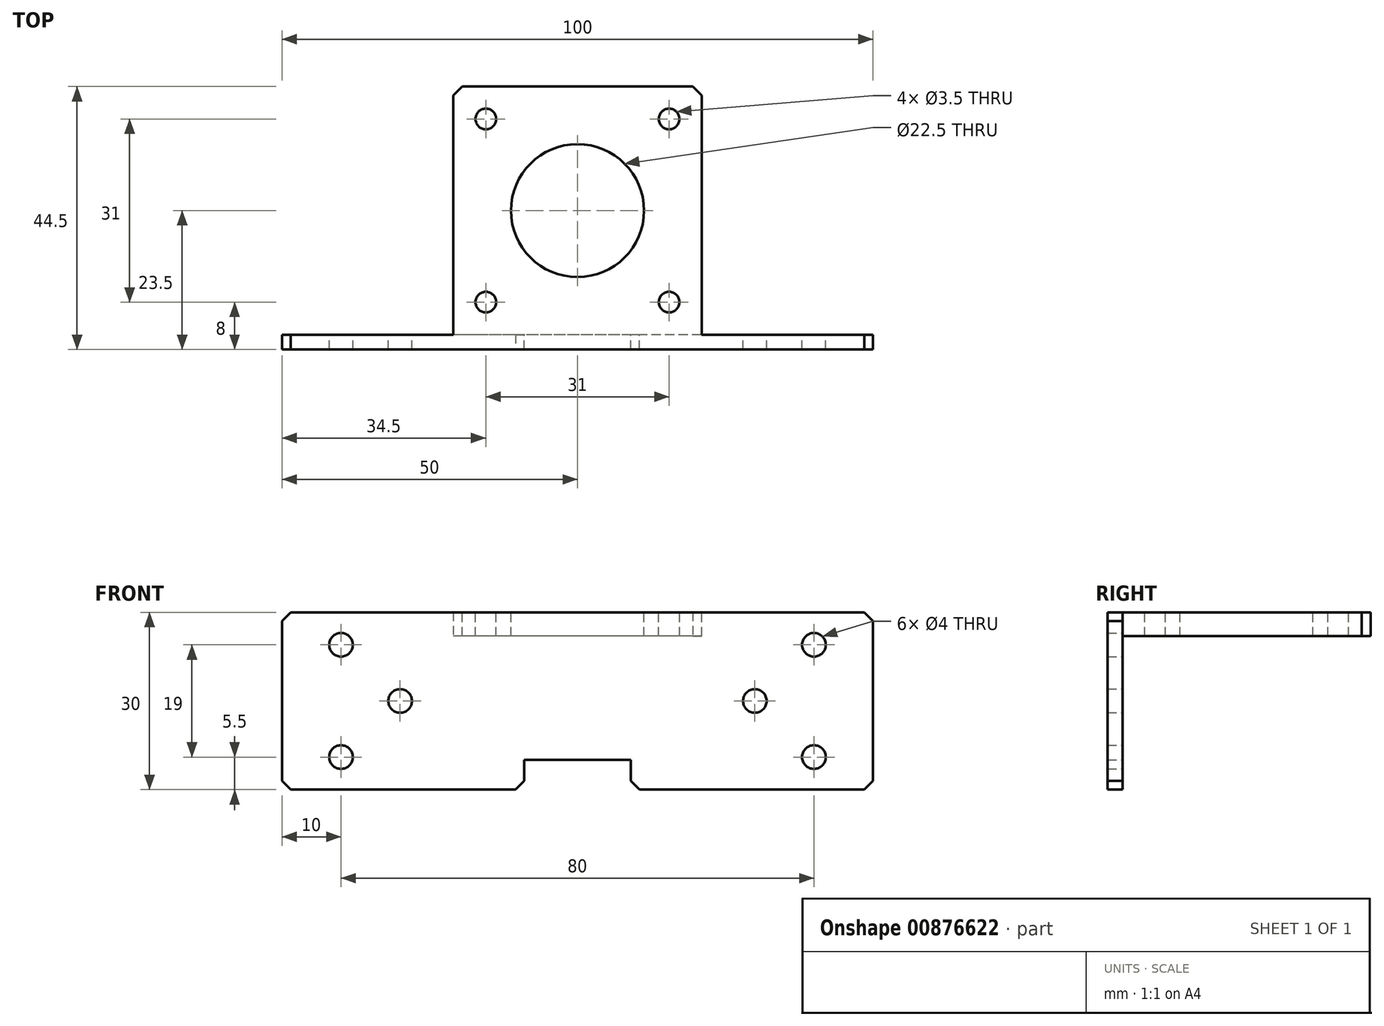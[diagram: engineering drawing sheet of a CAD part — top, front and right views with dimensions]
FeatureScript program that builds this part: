
annotation { "Feature Type Name" : "Feature", "Feature Type Description" : "" }
export const myFeature = defineFeature(function(context is Context, id is Id, definition is map)
    precondition{}
    {
        {
            var Q0;
            Q0=qCreatedBy(makeId("Top.planeOp"),FACE);
            var sketch = newSketch(context, id + "F0", { "sketchPlane" : qUnion([Q0])});
            skLineSegment(sketch, "E0.bottom", {"start": v(21, 21) * mm, "end": v(-21, 21) * mm});
            skLineSegment(sketch, "E0.top", {"start": v(21, -21) * mm, "end": v(-21, -21) * mm});
            skLineSegment(sketch, "E0.left", {"start": v(21, 21) * mm, "end": v(21, -21) * mm});
            skLineSegment(sketch, "E0.right", {"start": v(-21, 21) * mm, "end": v(-21, -21) * mm});
            skPoint(sketch, "E0.middle", {"position": v(0, 0) * mm});
            skLineSegment(sketch, "E1.0", {"start": v(21, 15.5) * mm, "end": v(-21, 15.5) * mm, "construction": true});
            skLineSegment(sketch, "E2.0", {"start": v(21, -15.5) * mm, "end": v(-21, -15.5) * mm, "construction": true});
            skLineSegment(sketch, "E3", {"start": v(-21, 0) * mm, "end": v(21, 0) * mm, "construction": true});
            skLineSegment(sketch, "E4", {"start": v(0, 21) * mm, "end": v(0, -21) * mm, "construction": true});
            skCircle(sketch, "E5", {"center": v(0, 0) * mm, "radius": 11.25 * mm});
            skLineSegment(sketch, "E6.0", {"start": v(-15.5, 21) * mm, "end": v(-15.5, -21) * mm, "construction": true});
            skLineSegment(sketch, "E7.0", {"start": v(15.5, 21) * mm, "end": v(15.5, -21) * mm, "construction": true});
            skCircle(sketch, "E8", {"center": v(-15.5, 15.5) * mm, "radius": 1.75 * mm});
            skCircle(sketch, "E9.MirrorC", {"center": v(15.5, 15.5) * mm, "radius": 1.75 * mm});
            skCircle(sketch, "E10.MirrorC", {"center": v(15.5, -15.5) * mm, "radius": 1.75 * mm});
            skCircle(sketch, "E11.MirrorC", {"center": v(-15.5, -15.5) * mm, "radius": 1.75 * mm});
            skSolve(sketch);
        }
        {
            var Q0;
            Q0=makeQuery(id+"F0.imprint","IMPRINT",FACE,{"disambiguationData":[TD([[makeQuery(id+"F0.imprint","IMPRINT",EDGE,{"derivedFrom":sQuery(id+"F0.wireOp",EDGE,"E0.bottom")}),1.0]])]});
            var Q1;
            Q1=makeQuery(id+"F0.imprint","IMPRINT",FACE,{"disambiguationData":[TD([[makeQuery(id+"F0.imprint","IMPRINT",EDGE,{"derivedFrom":sQuery(id+"F0.wireOp",EDGE,"HWjcr97h-bGiZ-oV4i-kZyB-UvR0nVrvKp9y")}),1.0]])]});
            extrude(context, id + "F1", {"entities" : qUnion([Q0, Q1]), "oppositeDirection" : true, "depth" : 4 * mm, "offsetDistance" : 25 * mm});
        }
        {
            var Q0;
            Q0=makeQuery(id+"F1.opExtrude","SWEPT_FACE",FACE,{"disambiguationData":[OSD([sQuery(id+"F0.wireOp",EDGE,"E0.top")])]});
            var sketch = newSketch(context, id + "F2", { "sketchPlane" : qUnion([Q0])});
            skLineSegment(sketch, "E12", {"start": v(0, 0) * mm, "end": v(0, -30) * mm, "construction": true});
            skLineSegment(sketch, "E13.bottom", {"start": v(50, 0) * mm, "end": v(-50, 0) * mm});
            skLineSegment(sketch, "E13.top", {"start": v(50, -30) * mm, "end": v(-50, -30) * mm});
            skLineSegment(sketch, "E13.left", {"start": v(50, 0) * mm, "end": v(50, -30) * mm});
            skLineSegment(sketch, "E13.right", {"start": v(-50, 0) * mm, "end": v(-50, -30) * mm});
            skPoint(sketch, "E13.middle", {"position": v(0, -15) * mm});
            skLineSegment(sketch, "E14.0", {"start": v(-40, 0) * mm, "end": v(-40, -30) * mm, "construction": true});
            skLineSegment(sketch, "E15.0", {"start": v(44, 0) * mm, "end": v(44, -30) * mm, "construction": true});
            skLineSegment(sketch, "E16.0", {"start": v(50, -5.5) * mm, "end": v(-50, -5.5) * mm, "construction": true});
            skLineSegment(sketch, "E17.0", {"start": v(70, -24.5) * mm, "end": v(-50, -24.5) * mm, "construction": true});
            skCircle(sketch, "E18", {"center": v(-40, -5.5) * mm, "radius": 2 * mm});
            skLineSegment(sketch, "E19", {"start": v(-50, -15) * mm, "end": v(50, -15) * mm, "construction": true});
            skCircle(sketch, "E20.MirrorC", {"center": v(40, -5.5) * mm, "radius": 2 * mm});
            skCircle(sketch, "E21.MirrorC", {"center": v(40, -24.5) * mm, "radius": 2 * mm});
            skCircle(sketch, "E22.MirrorC", {"center": v(-40, -24.5) * mm, "radius": 2 * mm});
            skLineSegment(sketch, "E23.0", {"start": v(-30, 0) * mm, "end": v(-30, -30) * mm, "construction": true});
            skCircle(sketch, "E24", {"center": v(-30, -15) * mm, "radius": 2 * mm});
            skCircle(sketch, "E25.MirrorC", {"center": v(30, -15) * mm, "radius": 2 * mm});
            skLineSegment(sketch, "E26.bottom", {"start": v(9, -25) * mm, "end": v(-9, -25) * mm});
            skLineSegment(sketch, "E26.left", {"start": v(9, -25) * mm, "end": v(9, -30) * mm});
            skLineSegment(sketch, "E26.right", {"start": v(-9, -25) * mm, "end": v(-9, -30) * mm});
            skPoint(sketch, "E26.middle", {"position": v(0, -30) * mm});
            skPoint(sketch, "E27", {"position": v(0, -25) * mm});
            skSolve(sketch);
        }
        {
            var Q0;
            {var subQ1=sQuery(id+"F2.wireOp",EDGE,"E13.left");Q0=makeQuery(id+"F2.imprint","IMPRINT",FACE,{"disambiguationData":[TD([[makeQuery(id+"F2.imprint","IMPRINT",EDGE,{"derivedFrom":subQ1}),-1.0]])]});}
            var Q1;
            {var subQ1=sQuery(id+"F0.wireOp",EDGE,"E0.top");Q1=makeQuery(id+"F2.imprint","IMPRINT",FACE,{"disambiguationData":[TD([[makeQuery(id+"F2.imprint","IMPRINT",EDGE,{"derivedFrom":makeQuery(id+"F1.opExtrude","CAP_EDGE",EDGE,{"disambiguationData":[OSD([subQ1])],"isStart":false})}),-1.0]])]});}
            extrude(context, id + "F3", {"entities" : qUnion([Q0, Q1]), "operationType" : NewBodyOperationType.ADD, "depth" : 2.5 * mm, "offsetDistance" : 25 * mm});
        }
        {
            var Q0;
            Q0=makeQuery(id+"F1.opExtrude","SWEPT_EDGE",EDGE,{"disambiguationData":[OSD([sQuery(id+"F0.wireOp",EDGE,"E0.bottom"),sQuery(id+"F0.wireOp",EDGE,"E0.right")])]});
            var Q1;
            Q1=makeQuery(id+"F1.opExtrude","SWEPT_EDGE",EDGE,{"disambiguationData":[OSD([sQuery(id+"F0.wireOp",EDGE,"E0.bottom"),sQuery(id+"F0.wireOp",EDGE,"E0.left")])]});
            var Q2;
            Q2=makeQuery(id+"F3.opExtrude","SWEPT_EDGE",EDGE,{"disambiguationData":[OSD([sQuery(id+"F2.wireOp",EDGE,"E13.bottom"),sQuery(id+"F2.wireOp",EDGE,"E13.right")])]});
            var Q3;
            Q3=makeQuery(id+"F3.opExtrude","SWEPT_EDGE",EDGE,{"disambiguationData":[OSD([sQuery(id+"F2.wireOp",EDGE,"E13.top"),sQuery(id+"F2.wireOp",EDGE,"E13.right")])]});
            var Q4;
            Q4=makeQuery(id+"F3.opExtrude","SWEPT_EDGE",EDGE,{"disambiguationData":[OSD([sQuery(id+"F2.wireOp",EDGE,"E13.top"),sQuery(id+"F2.wireOp",EDGE,"E13.left")])]});
            var Q5;
            Q5=makeQuery(id+"F3.opExtrude","SWEPT_EDGE",EDGE,{"disambiguationData":[OSD([sQuery(id+"F2.wireOp",EDGE,"E13.bottom"),sQuery(id+"F2.wireOp",EDGE,"E13.left")])]});
            var Q6;
            Q6=makeQuery(id+"F3.opExtrude","SWEPT_EDGE",EDGE,{"disambiguationData":[OSD([sQuery(id+"F2.wireOp",EDGE,"E13.top"),sQuery(id+"F2.wireOp",EDGE,"E26.right")])]});
            var Q7;
            Q7=makeQuery(id+"F3.opExtrude","SWEPT_EDGE",EDGE,{"disambiguationData":[OSD([sQuery(id+"F2.wireOp",EDGE,"E13.top"),sQuery(id+"F2.wireOp",EDGE,"E26.left")])]});
            chamfer(context, id + "F4", {"entities" : qUnion([Q0, Q1, Q2, Q3, Q4, Q5, Q6, Q7]), "width" : 1.5 * mm, "tangentPropagation" : true});
        }
    });
